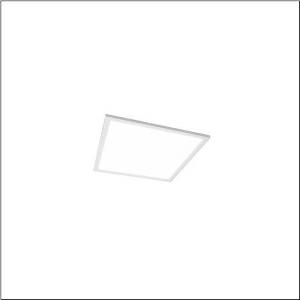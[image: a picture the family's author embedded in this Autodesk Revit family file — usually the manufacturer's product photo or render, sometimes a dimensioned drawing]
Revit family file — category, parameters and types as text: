
# Revit family: apollon_21_square_51mq13wd2414
name_source: partatom
category: Lighting Fixtures
units: mm (PartAtom-declared; Revit-internal decimal feet)

## family parameters
Cut with Voids When Loaded = No
Host = Face
Light Source = No
Part Type = Normal
Room Calculation Point = No
Round Connector Dimension = Use Diameter
Shared = No

## types (1)
- Apollon 21 square (1 x LED, 1800 lm, 14 W, 4000K)
    Apparent Load = 14 VA
    CIE Flux Codes = 68 89 97 100 100
    Color Rendering = 80
    Color Temperature = 4000K
    Default Elevation = 1800 mm  [stored 5.90551 ft]
    Description = Apollon 21 square, office luminaire, primary optical cover: micro prismatic cover, of PMMA, CAT 2 (L<= 3000cd/m²), light emission: direct distribution, primary light characteristic: symmetric, installation type: recessed, LED, rated luminous flux: 1.800lm, luminous efficacy: 129lm/W, light colour: 840, colour temperature: 4000K, control gear: DALI 2, Multilumen, with terminal, 5-pole, mains connection: 220..240V, AC/DC, 0/50..60Hz, rated input power: 14W, housing, of sheet steel, coated, traffic white (RAL 9016), length: 296mm, width: 296mm, height: 55mm, recess depth: 180mm, housing upper side, of sheet steel, galvanised, protection rating (complete): IP20, protection rating (lamp compartment, on room side): IP50, insulation class (complete): insulation class II (safety insulation), certification: CE, ENEC, impact resistance: IK03, permissible operating ambient temperature: -20..+45°C, permissible storage temperature: -40..+80°C, standard: EN 60598-2-22, packaging unit: 1 piece
    Height = 0 mm  [stored 0 ft]
    Lamp = 1 x LED
    Lamp Light Flux = 1800 lm
    Lamp Power = 14 W
    Lamp count = 1
    Length = 295 mm
    Luminous efficacy = 129 lm/W
    Manufacturer = Siteco
    ModVariant = No
    Model = 51MQ13WD2414
    Mounting Place = Ceiling
    Mounting Type = Recessed
    Number of Poles = 1
    OnlyDefault = Yes
    Power Factor = 1
    Product Name = Apollon 21 square
    Product group = office luminaire | ceiling recessed
    ProductGroupID = 401
    Protection Class = Protection class II
    Protection Degree = IP 20
    RLX_Detail_Level = 1
    RLX_Emergency_Light_Flux = 0 lm
    RLX_Emergency_Type = 0
    RLX_Emergency_Type_DB = No
    RlxData = <blob elided: 9309 chars, md5=3aa346be>
    Socket = socket
    Standby Power = 0 W
    System Light Flux = 1800 lm
    System Power = 14 W
    Type Comments = Product without accessories
    Type Image = l_1291030.jpg
    URL = http://relux.com
    VarID = ---
    Voltage = 0 V
    Weight = 0.00 kg
    Width = 295 mm

note: [stored X ft] marks values corroborated as IEEE doubles in the binary element streams (Revit-internal decimal feet)

## geometry (parser evidence)
native form markers: Sweep x10
no freeform markers — native parametric forms only
